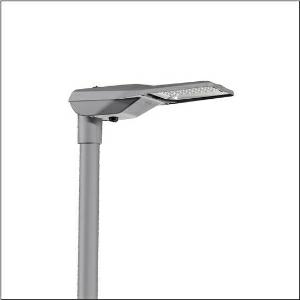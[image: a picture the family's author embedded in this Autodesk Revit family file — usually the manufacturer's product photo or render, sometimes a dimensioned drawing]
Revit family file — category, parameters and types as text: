
# Revit family: streetlight_sl_21_mini___st1_5a_5xe2p43t08gb_00fd
name_source: partatom
category: Lighting Fixtures
units: mm (PartAtom-declared; Revit-internal decimal feet)

## family parameters
Cut with Voids When Loaded = No
Host = Face
Light Source = No
Part Type = Normal
Room Calculation Point = No
Round Connector Dimension = Use Diameter
Shared = No

## types (1)
- --- (1 x LED, 6080 lm, 40.4 W, 4000K)
    Apparent Load = 40 VA
    CIE Flux Codes = 22 53 95 100 100
    Color Rendering = 70
    Color Temperature = 4000K
    Default Elevation = 1800 mm
    Description = Streetlight SL 21 mini, mast luminaire, primary light control with lens, of PMMA, primary optical cover: cover, of toughened safety glass, transparent, light distribution: ST1.5a, light emission: direct distribution, primary light characteristic: asymmetric, installation type: side-entry, post-top, LED, High Power LED, rated luminous flux: 6.080lm, luminous efficacy: 151lm/W, light colour: 740, colour temperature: 4000K, control gear: D4i, control: overheat protection, constant luminous flux control, time-dependent luminous flux control, flexible luminous flux parameterisation, pre-setting: logarithmic dimming characteristic, mains connection: 220..240V, AC, 50/60Hz, start of lifetime: 40W, end of service life: 41W, reduction: 19W, luminaire housing, of diecast aluminium, powder-coated, Siteco® metallic grey (DB 702S), corrosivity category C5 mid according to DIN EN ISO 12944, please order mast flange separately, inclination adjustable: 0°, 5°, 10°, 15°, sealing non-destructively replaceable, multi-level sealing system, length: 628mm, width: 235mm, height: 110mm, mast flange for spigot size: 42mm (side-entry): 5XC10008XM4, 60/48mm (side-entry/post-top): 5XC10108XM2, 76/60mm (side-entry/post-top): 5XC10108XM1, mounting height: 4..8m, Smart Interface below and above, protection rating (complete): IP66, insulation class (complete): insulation class II (safety insulation), certification: CE, ENEC, ENEC+, VDE, impact resistance: IK10, permissible operating ambient temperature for outdoor applications: -40..+50°C, standard-compliant lighting for roads and squares, packaging unit: 1 piece

Light Distribution: ST1.5a
    Height = 110 mm
    Lamp = 1 x LED
    Lamp Light Flux = 6080 lm
    Lamp Power = 40.4 W
    Lamp count = 1
    Length = 625 mm
    Luminous efficacy = 151 lm/W
    Manufacturer = Siteco
    ModVariant = No
    Model = 5XE2P43T08GB
    Number of Poles = 1
    OnlyDefault = Yes
    Power Factor = 1
    Product Name = Streetlight SL 21 mini | ST1.5a
    Product group = mast luminaire | pylon top
    ProductGroupID = 6100
    Protection Class = Protection class II
    Protection Degree = IP 66
    RLX_Detail_Level = 1
    RLX_Emergency_Light_Flux = 0 lm
    RLX_Emergency_Type = 0
    RLX_Emergency_Type_DB = No
    RlxData = <blob elided: 29817 chars, md5=a2ac1547>
    Socket = socket
    Standby Power = 0 W
    System Light Flux = 6080 lm
    System Power = 40 W
    Type Comments = factory setting: luminous flux: 100 % | dim-lin: 254 | 812 mA
    Type Image = l_1003514.jpg
    URL = http://relux.com
    VarID = @adj_175528
    Voltage = 0 V
    Weight = 0.00 kg
    Width = 234 mm

## geometry (parser evidence)
native form markers: Blend x4, Sweep x9
no freeform markers — native parametric forms only
